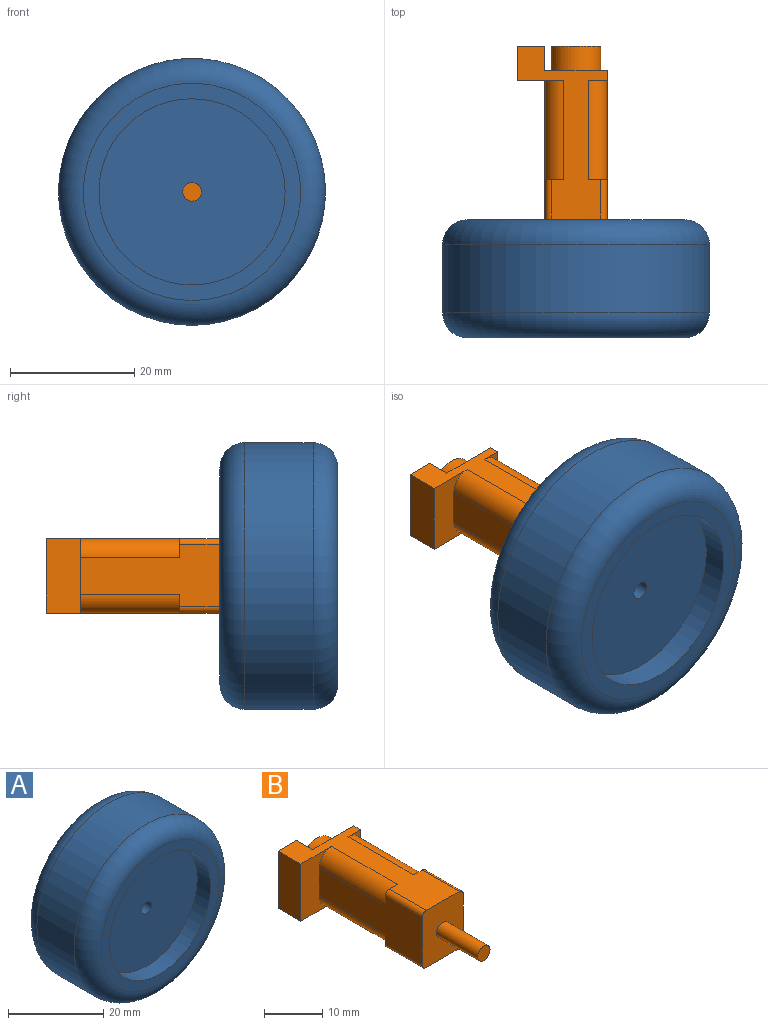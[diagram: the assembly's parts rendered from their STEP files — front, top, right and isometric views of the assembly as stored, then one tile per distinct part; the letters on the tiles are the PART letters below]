
ASSEMBLY  parts=2 mates=1
PART A: 10 faces, bbox 46.5x19x46.5 mm
  f0: cylinder r=21.5mm len=43mm, axis (0,1,0), area 1486mm2, adj f3,f4
  f1: plane 35x35mm, normal (0,-1,0), area 255.3mm2, adj f4,f5
  f2: plane 35x35mm, normal (0,1,0), area 255.3mm2, adj f3,f7
  f3: torus R=17.5mm, axis (0,-1,0), area 791.4mm2, adj f0,f2
  f4: torus R=17.5mm, axis (0,-1,0), area 791.4mm2, adj f0,f1
  f5: cylinder r=15mm len=30mm, axis (0,-1,0), area 377mm2, adj f1,f6
  f6: plane 30x30mm, normal (0,-1,0), area 699.8mm2, adj f5,f9
  f7: cylinder r=15mm len=30mm, axis (0,1,0), area 377mm2, adj f2,f8
  f8: plane 30x30mm, normal (0,1,0), area 699.8mm2, adj f7,f9
  f9: cylinder r=1.5mm len=11mm, axis (0,-1,0), area 103.7mm2, adj f6,f8
PART B: 28 faces, bbox 14.5x40.5x12 mm
  f0: plane 12x10mm, normal (0,1,0), area 69.7mm2, adj f1,f3,f4,f22,f24
  f1: plane 30.5x14.5mm, normal (0,0,1), area 176.8mm2, adj f0,f4,f5,f8,f9,f12,f13,f16
  f2: plane 25x10mm, normal (-1,0,0), area 186mm2, adj f5,f6,f9,f10,f12,f14,f16,f21
  f3: plane 30.5x14.5mm, normal (0,0,-1), area 176.8mm2, adj f0,f4,f6,f7,f10,f11,f12,f14
  f4: plane 26.6x12mm, normal (1,0,0), area 205.2mm2, adj f0,f1,f3,f7,f8,f11,f12,f13
  f5: cylinder r=3mm len=16mm, axis (0,1,0), area 75.4mm2, adj f1,f2,f9,f21
  f6: cylinder r=3mm len=16mm, axis (0,-1,0), area 75.4mm2, adj f2,f3,f10,f21
  f7: cylinder r=3mm len=16mm, axis (0,1,0), area 75.4mm2, adj f3,f4,f11,f19
  f8: cylinder r=3mm len=16mm, axis (0,-1,0), area 75.4mm2, adj f1,f4,f13,f18
  f9: plane 3x3mm, normal (0,1,0), area 1.7mm2, adj f1,f2,f5,f16
  f10: plane 3x3mm, normal (0,1,0), area 1.7mm2, adj f2,f3,f6,f14
  f11: plane 3x3mm, normal (0,1,0), area 1.7mm2, adj f3,f4,f7,f15
  f12: plane 12x10mm, normal (0,-1,0), area 112.1mm2, adj f1,f2,f3,f4,f14,f15,f16,f17
  f13: plane 3x3mm, normal (0,1,0), area 1.7mm2, adj f1,f4,f8,f17
  f14: cylinder r=1mm len=9mm, axis (0,-1,0), area 14.1mm2, adj f2,f3,f10,f12
  f15: cylinder r=1mm len=9mm, axis (0,1,0), area 14.1mm2, adj f3,f4,f11,f12
  f16: cylinder r=1mm len=9mm, axis (0,1,0), area 14.1mm2, adj f1,f2,f9,f12
  f17: cylinder r=1mm len=9mm, axis (0,-1,0), area 14.1mm2, adj f1,f4,f12,f13
  f18: plane 3x3mm, normal (0,-1,0), area 1.9mm2, adj f1,f4,f8
  f19: plane 3x3mm, normal (0,-1,0), area 1.9mm2, adj f3,f4,f7
  f20: plane 12x5.5mm, normal (-1,0,0), area 66mm2, adj f1,f3,f21,f25
  f21: plane 12x7.5mm, normal (0,-1,0), area 57.9mm2, adj f1,f2,f3,f5,f6,f20
  f22: cylinder r=4mm len=8mm, axis (0,-1,0), area 98mm2, adj f0,f23
  f23: plane 8x8mm, normal (0,1,0), area 50.3mm2, adj f22
  f24: plane 12x3.9mm, normal (1,0,0), area 46.8mm2, adj f0,f1,f3,f25
  f25: plane 12x4.5mm, normal (0,1,0), area 54mm2, adj f1,f3,f20,f24
  f26: cylinder r=1.5mm len=10mm, axis (0,1,0), area 94.2mm2, adj f12,f27
  f27: plane 3x3mm, normal (0,-1,0), area 7.1mm2, adj f26
PLACE A t=(1.55,15.42,-6.81)mm
PLACE B t=(-3.45,37.92,-12.81)mm
MATE revolute B.f22 <-> A.f0  axis (0,1,0) through (1.55,7.92,-6.81)mm
